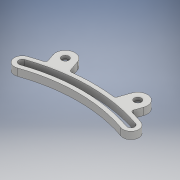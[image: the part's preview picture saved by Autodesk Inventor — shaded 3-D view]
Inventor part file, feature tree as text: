
AUTODESK INVENTOR PART (.ipt)
format: ipt  version: 2017 (Build 210142000, 142)  size: 173,568 bytes
history: native  units: mm
features: sketch x2, extrude x2, hole x1, mirror x1, fillet x1
ambient origin geometry x8: Origin, YZ Plane, XZ Plane, XY Plane, X Axis, Y Axis, Z Axis, Center Point
bodies: Body1 (feature_tree)
feature tree (7):
  sketch  "Sketch3"  dims[d32=153.0mm d33=8.0mm d34=3.25mm d35=45.0mm d36=22.5mm d37=3.0mm d38=8.0mm d39=15.0mm d40=0.0mm d41=71.75mm d42=3.0mm d43=0.0mm]
  extrude  "Extrusion4"  Depth=3.0mm TaperAngle=0.0deg
  extrude  "Extrusion5"  Depth=1.0mm
  hole  "Hole1"  [1 undecoded]
  mirror  "Mirror1"
  fillet  "Fillet1"  [1 undecoded]
  sketch  "Sketch5"  dims[d44=3.0mm d45=0.0mm d46=3.0mm d47=0.0mm d48=4.0mm d49=3.0mm d50=6.0mm d51=6.5mm d52=2.0mm d53=90.0deg d54=8.0mm d55=20.594885mm d56=1.0mm]
note: 2 required parameter values undecoded (feature->parameter linkage not recoverable at this tier; creation-order binding heuristic only, values carry confidence <= 0.55)
